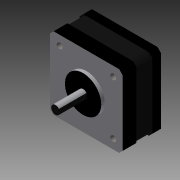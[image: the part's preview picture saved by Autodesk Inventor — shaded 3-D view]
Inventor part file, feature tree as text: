
AUTODESK INVENTOR PART (.ipt)
format: ipt  version: 2020 (Build 240168000, 168)  size: 207,872 bytes
history: native  units: in
note: dims shown in document units (in); Inventor stores cm internally (conversion verified against a paired STEP export)
features: extrude x5, sketch x5, other x2, projected_geometry x2, imported_body x1
ambient origin geometry x8: Origin, YZ Plane, XZ Plane, XY Plane, X Axis, Y Axis, Z Axis, Center Point
bodies: Body1 (feature_tree)
feature tree (15):
  other  "Cut-Extrude6"
  other  "stepper (hardware)1"
  extrude  "Extrusion1"  Depth=0.4724in TaperAngle=0.0deg
  extrude  "Extrusion2"  Depth=0.4724in TaperAngle=0.0deg
  extrude  "Extrusion3"  Depth=0.3543in TaperAngle=0.0deg
  extrude  "Extrusion4"  [1 undecoded]
  extrude  "Extrusion5"  [1 undecoded]
  imported_body  "Base1"
  sketch  "Sketch2"  dims[d0=0.1969in d1=0.0in d2=0.4724in d3=0.0in]
  sketch  "Sketch3"  dims[d4=0.4724in d5=0.0in d6=0.3543in d7=0.0in]
  projected_geometry  "Projected Loop1"
  sketch  "Sketch4"  dims[d8=0.1772in d9=0.3543in d10=0.0in]
  projected_geometry  "Projected Loop2"
  sketch  "Sketch5"
  sketch  "Sketch6"
note: 2 required parameter values undecoded (feature->parameter linkage not recoverable at this tier; creation-order binding heuristic only, values carry confidence <= 0.55)
